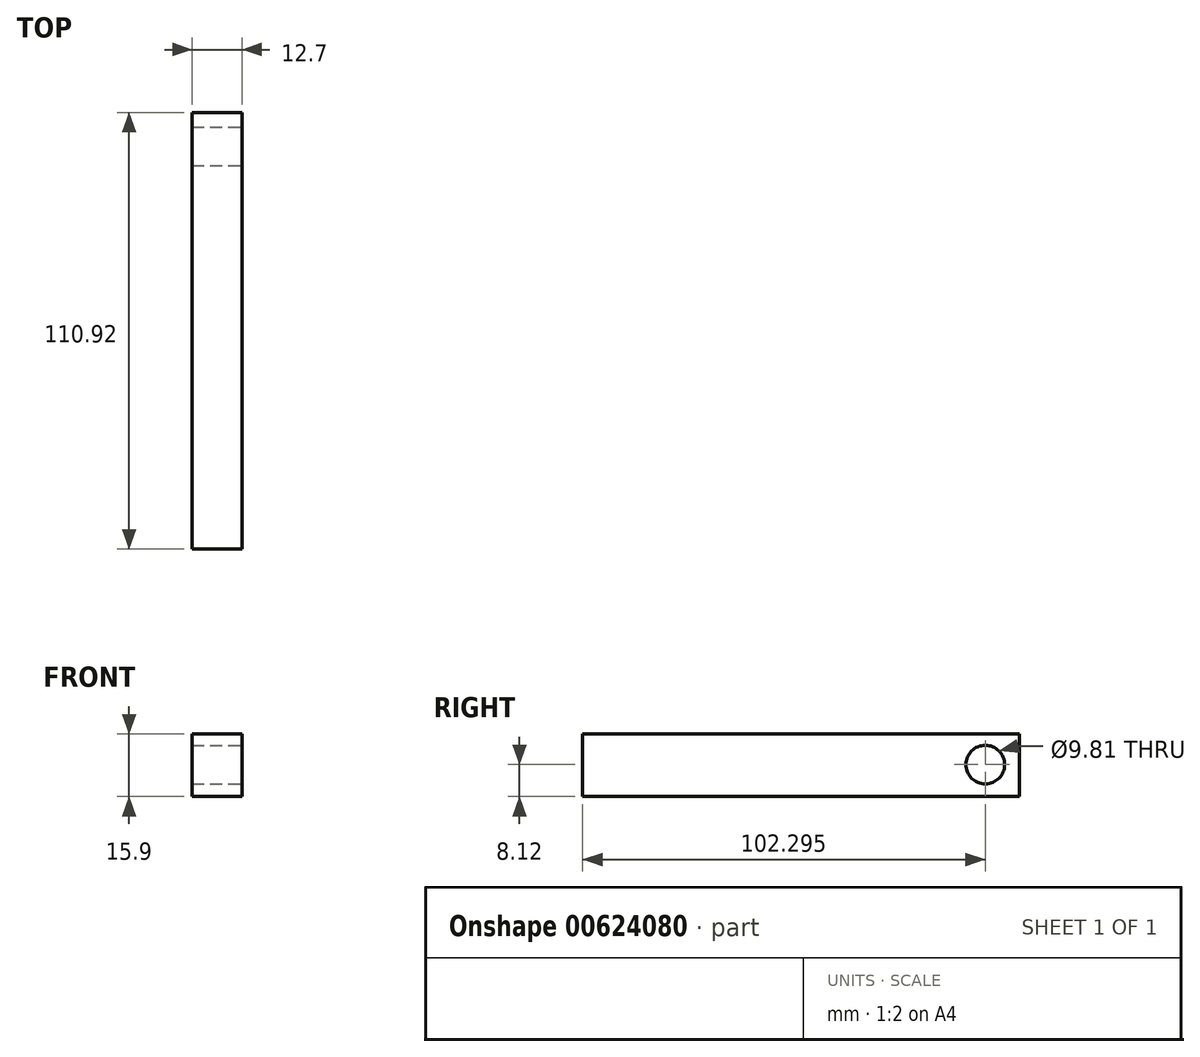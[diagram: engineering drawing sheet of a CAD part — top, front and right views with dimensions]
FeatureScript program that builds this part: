
annotation { "Feature Type Name" : "Feature", "Feature Type Description" : "" }
export const myFeature = defineFeature(function(context is Context, id is Id, definition is map)
    precondition{}
    {
        {
            var Q0;
            Q0=qCreatedBy(makeId("Right.planeOp"),FACE);
            var sketch = newSketch(context, id + "F0", { "sketchPlane" : qUnion([Q0])});
            skLineSegment(sketch, "E0", {"start": v(50.22, 7.78) * mm, "end": v(-60.7, 7.78) * mm});
            skLineSegment(sketch, "E1", {"start": v(-60.7, 7.78) * mm, "end": v(-60.7, -8.12) * mm});
            skLineSegment(sketch, "E2", {"start": v(-60.7, -8.12) * mm, "end": v(50.22, -8.12) * mm});
            skLineSegment(sketch, "E3", {"start": v(50.22, -8.12) * mm, "end": v(50.22, 7.78) * mm});
            skSolve(sketch);
        }
        {
            var Q0;
            Q0 = qSketchRegion(id + "F0", true);
            extrude(context, id + "F1", {"entities" : qUnion([Q0]), "depth" : 12.7 * mm, "offsetDistance" : 25.4 * mm});
        }
        {
            var Q0;
            Q0=makeQuery(id+"F1.opExtrude","CAP_FACE",FACE,{"disambiguationData":[OSD([sQuery(id+"F0.wireOp",EDGE,"E0"),sQuery(id+"F0.wireOp",EDGE,"E1"),sQuery(id+"F0.wireOp",EDGE,"E2"),sQuery(id+"F0.wireOp",EDGE,"E3")])],"isStart":false});
            var sketch = newSketch(context, id + "F2", { "sketchPlane" : qUnion([Q0])});
            skCircle(sketch, "E4", {"center": v(41.6, 0) * mm, "radius": 4.9 * mm});
            skSolve(sketch);
        }
        {
            var Q0;
            Q0 = qSketchRegion(id + "F2", true);
            extrude(context, id + "F3", {"entities" : qUnion([Q0]), "operationType" : NewBodyOperationType.REMOVE, "endBound" : BoundingType.THROUGH_ALL, "oppositeDirection" : true, "depth" : 25.4 * mm, "offsetDistance" : 25.4 * mm});
        }
    });
